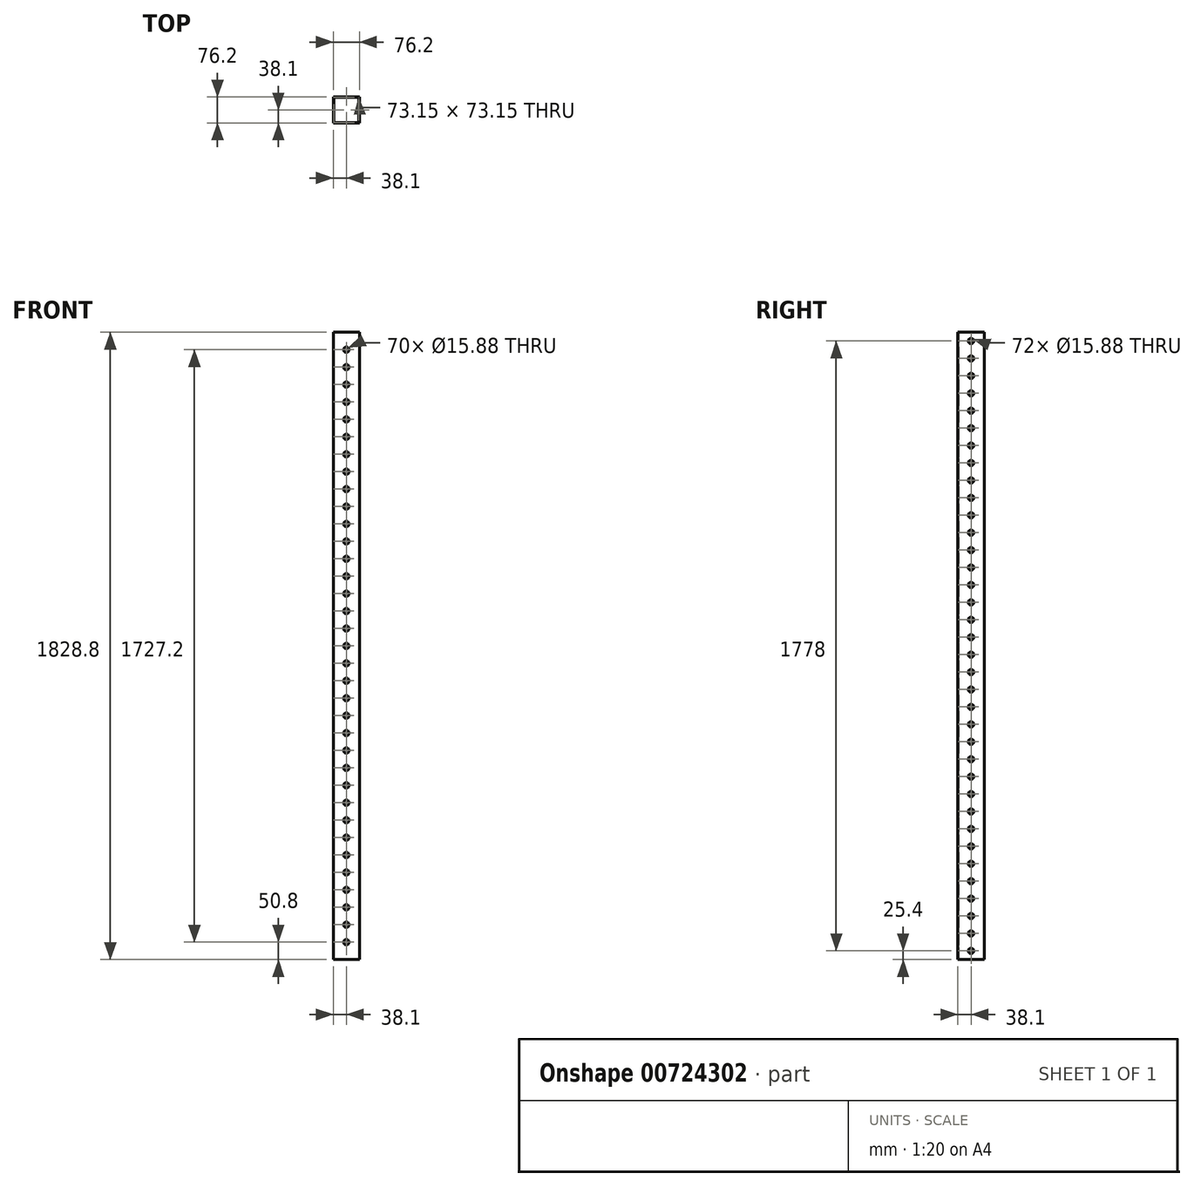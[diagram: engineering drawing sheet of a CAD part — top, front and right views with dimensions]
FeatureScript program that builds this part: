
annotation { "Feature Type Name" : "Feature", "Feature Type Description" : "" }
export const myFeature = defineFeature(function(context is Context, id is Id, definition is map)
    precondition{}
    {
        {
            var Q0;
            Q0=qCreatedBy(makeId("Top.planeOp"),FACE);
            var sketch = newSketch(context, id + "F0", { "sketchPlane" : qUnion([Q0])});
            skLineSegment(sketch, "E0.bottom", {"start": v(-38.1, -38.1) * mm, "end": v(38.1, -38.1) * mm});
            skLineSegment(sketch, "E0.top", {"start": v(-38.1, 38.1) * mm, "end": v(38.1, 38.1) * mm});
            skLineSegment(sketch, "E0.left", {"start": v(-38.1, -38.1) * mm, "end": v(-38.1, 38.1) * mm});
            skLineSegment(sketch, "E0.right", {"start": v(38.1, -38.1) * mm, "end": v(38.1, 38.1) * mm});
            skPoint(sketch, "E0.middle", {"position": v(0, 0) * mm});
            skLineSegment(sketch, "E1.bottom", {"start": v(-36.58, -36.58) * mm, "end": v(36.58, -36.58) * mm});
            skLineSegment(sketch, "E1.top", {"start": v(-36.58, 36.58) * mm, "end": v(36.58, 36.58) * mm});
            skLineSegment(sketch, "E1.left", {"start": v(-36.58, -36.58) * mm, "end": v(-36.58, 36.58) * mm});
            skLineSegment(sketch, "E1.right", {"start": v(36.58, -36.58) * mm, "end": v(36.58, 36.58) * mm});
            skSolve(sketch);
        }
        {
            var Q0;
            Q0=makeQuery(id+"F0.imprint","IMPRINT",FACE,{"disambiguationData":[TD([[makeQuery(id+"F0.imprint","IMPRINT",EDGE,{"derivedFrom":sQuery(id+"F0.wireOp",EDGE,"E0.bottom")}),1.0]])]});
            extrude(context, id + "F1", {"entities" : qUnion([Q0]), "depth" : 1828.8 * mm, "offsetDistance" : 25.4 * mm});
        }
        {
            var Q0;
            Q0=qCreatedBy(makeId("Front.planeOp"),FACE);
            cPlane(context, id + "F2", {"entities" : qUnion([Q0]), "cplaneType" : CPlaneType.OFFSET, "offset" : 76.2 * mm, "width" : 152.4 * mm, "height" : 152.4 * mm});
        }
        {
            var Q0;
            Q0=qCreatedBy(id+"F2.planeOp",FACE);
            var sketch = newSketch(context, id + "F3", { "sketchPlane" : qUnion([Q0])});
            skPoint(sketch, "E2", {"position": v(0, 50.8) * mm});
            skPoint(sketch, "E3.1.0.0", {"position": v(0, 101.6) * mm});
            skPoint(sketch, "E3.2.0.0", {"position": v(0, 152.4) * mm});
            skPoint(sketch, "E3.3.0.0", {"position": v(0, 203.2) * mm});
            skPoint(sketch, "E3.4.0.0", {"position": v(0, 254) * mm});
            skPoint(sketch, "E3.5.0.0", {"position": v(0, 304.8) * mm});
            skPoint(sketch, "E3.6.0.0", {"position": v(0, 355.6) * mm});
            skPoint(sketch, "E3.7.0.0", {"position": v(0, 406.4) * mm});
            skPoint(sketch, "E3.8.0.0", {"position": v(0, 457.2) * mm});
            skPoint(sketch, "E3.9.0.0", {"position": v(0, 508) * mm});
            skPoint(sketch, "E3.10.0.0", {"position": v(0, 558.8) * mm});
            skPoint(sketch, "E3.11.0.0", {"position": v(0, 609.6) * mm});
            skPoint(sketch, "E3.12.0.0", {"position": v(0, 660.4) * mm});
            skPoint(sketch, "E3.13.0.0", {"position": v(0, 711.2) * mm});
            skPoint(sketch, "E3.14.0.0", {"position": v(0, 762) * mm});
            skPoint(sketch, "E3.15.0.0", {"position": v(0, 812.8) * mm});
            skPoint(sketch, "E3.16.0.0", {"position": v(0, 863.6) * mm});
            skLineSegment(sketch, "E3.direction1", {"start": v(0, 50.8) * mm, "end": v(0, 101.6) * mm, "construction": true});
            skPoint(sketch, "E4.0.17.0", {"position": v(0, 914.4) * mm});
            skPoint(sketch, "E4.0.18.0", {"position": v(0, 965.2) * mm});
            skPoint(sketch, "E4.0.19.0", {"position": v(0, 1016) * mm});
            skPoint(sketch, "E4.0.20.0", {"position": v(0, 1066.8) * mm});
            skPoint(sketch, "E4.0.21.0", {"position": v(0, 1117.6) * mm});
            skPoint(sketch, "E4.0.22.0", {"position": v(0, 1168.4) * mm});
            skPoint(sketch, "E4.0.23.0", {"position": v(0, 1219.2) * mm});
            skPoint(sketch, "E4.0.24.0", {"position": v(0, 1270) * mm});
            skPoint(sketch, "E4.0.25.0", {"position": v(0, 1320.8) * mm});
            skPoint(sketch, "E4.0.26.0", {"position": v(0, 1371.6) * mm});
            skPoint(sketch, "E4.0.27.0", {"position": v(0, 1422.4) * mm});
            skPoint(sketch, "E4.0.28.0", {"position": v(0, 1473.2) * mm});
            skPoint(sketch, "E4.0.29.0", {"position": v(0, 1524) * mm});
            skPoint(sketch, "E4.0.30.0", {"position": v(0, 1574.8) * mm});
            skPoint(sketch, "E4.0.31.0", {"position": v(0, 1625.6) * mm});
            skPoint(sketch, "E4.0.32.0", {"position": v(0, 1676.4) * mm});
            skPoint(sketch, "E4.0.33.0", {"position": v(0, 1727.2) * mm});
            skPoint(sketch, "E5.0.34.0", {"position": v(0, 1778) * mm});
            skSolve(sketch);
        }
        {
            var Q0;
            Q0=qCreatedBy(makeId("Right.planeOp"),FACE);
            cPlane(context, id + "F4", {"entities" : qUnion([Q0]), "cplaneType" : CPlaneType.OFFSET, "offset" : 76.2 * mm, "width" : 152.4 * mm, "height" : 152.4 * mm});
        }
        {
            var Q0;
            Q0=qCreatedBy(id+"F4.planeOp",FACE);
            var sketch = newSketch(context, id + "F5", { "sketchPlane" : qUnion([Q0])});
            skPoint(sketch, "E6", {"position": v(0, 25.4) * mm});
            skPoint(sketch, "E7.1.0.0", {"position": v(0, 76.2) * mm});
            skPoint(sketch, "E7.2.0.0", {"position": v(0, 127) * mm});
            skPoint(sketch, "E7.3.0.0", {"position": v(0, 177.8) * mm});
            skPoint(sketch, "E7.4.0.0", {"position": v(0, 228.6) * mm});
            skPoint(sketch, "E7.5.0.0", {"position": v(0, 279.4) * mm});
            skPoint(sketch, "E7.6.0.0", {"position": v(0, 330.2) * mm});
            skPoint(sketch, "E7.7.0.0", {"position": v(0, 381) * mm});
            skPoint(sketch, "E7.8.0.0", {"position": v(0, 431.8) * mm});
            skPoint(sketch, "E7.9.0.0", {"position": v(0, 482.6) * mm});
            skPoint(sketch, "E7.10.0.0", {"position": v(0, 533.4) * mm});
            skPoint(sketch, "E7.11.0.0", {"position": v(0, 584.2) * mm});
            skPoint(sketch, "E7.12.0.0", {"position": v(0, 635) * mm});
            skPoint(sketch, "E7.13.0.0", {"position": v(0, 685.8) * mm});
            skPoint(sketch, "E7.14.0.0", {"position": v(0, 736.6) * mm});
            skPoint(sketch, "E7.15.0.0", {"position": v(0, 787.4) * mm});
            skPoint(sketch, "E7.16.0.0", {"position": v(0, 838.2) * mm});
            skPoint(sketch, "E7.17.0.0", {"position": v(0, 889) * mm});
            skLineSegment(sketch, "E7.direction1", {"start": v(0, 25.4) * mm, "end": v(0, 76.2) * mm, "construction": true});
            skPoint(sketch, "E8.0.18.0", {"position": v(0, 939.8) * mm});
            skPoint(sketch, "E8.0.19.0", {"position": v(0, 990.6) * mm});
            skPoint(sketch, "E8.0.20.0", {"position": v(0, 1041.4) * mm});
            skPoint(sketch, "E8.0.21.0", {"position": v(0, 1092.2) * mm});
            skPoint(sketch, "E8.0.22.0", {"position": v(0, 1143) * mm});
            skPoint(sketch, "E8.0.23.0", {"position": v(0, 1193.8) * mm});
            skPoint(sketch, "E8.0.24.0", {"position": v(0, 1244.6) * mm});
            skPoint(sketch, "E8.0.25.0", {"position": v(0, 1295.4) * mm});
            skPoint(sketch, "E8.0.26.0", {"position": v(0, 1346.2) * mm});
            skPoint(sketch, "E8.0.27.0", {"position": v(0, 1397) * mm});
            skPoint(sketch, "E8.0.28.0", {"position": v(0, 1447.8) * mm});
            skPoint(sketch, "E8.0.29.0", {"position": v(0, 1498.6) * mm});
            skPoint(sketch, "E8.0.30.0", {"position": v(0, 1549.4) * mm});
            skPoint(sketch, "E8.0.31.0", {"position": v(0, 1600.2) * mm});
            skPoint(sketch, "E8.0.32.0", {"position": v(0, 1651) * mm});
            skPoint(sketch, "E8.0.33.0", {"position": v(0, 1701.8) * mm});
            skPoint(sketch, "E8.0.34.0", {"position": v(0, 1752.6) * mm});
            skPoint(sketch, "E8.0.35.0", {"position": v(0, 1803.4) * mm});
            skSolve(sketch);
        }
        {
            var Q0;
            Q0=sQuery(id+"F5.wireOp",VERTEX,"E6");
            var Q1;
            Q1=sQuery(id+"F5.wireOp",VERTEX,"E7.1.0.0");
            var Q2;
            Q2=sQuery(id+"F5.wireOp",VERTEX,"E7.2.0.0");
            var Q3;
            Q3=sQuery(id+"F5.wireOp",VERTEX,"E7.3.0.0");
            var Q4;
            Q4=sQuery(id+"F5.wireOp",VERTEX,"E7.4.0.0");
            var Q5;
            Q5=sQuery(id+"F5.wireOp",VERTEX,"E7.5.0.0");
            var Q6;
            Q6=sQuery(id+"F5.wireOp",VERTEX,"E7.6.0.0");
            var Q7;
            Q7=sQuery(id+"F5.wireOp",VERTEX,"E7.7.0.0");
            var Q8;
            Q8=sQuery(id+"F5.wireOp",VERTEX,"E7.8.0.0");
            var Q9;
            Q9=sQuery(id+"F5.wireOp",VERTEX,"E7.9.0.0");
            var Q10;
            Q10=sQuery(id+"F5.wireOp",VERTEX,"E7.10.0.0");
            var Q11;
            Q11=sQuery(id+"F5.wireOp",VERTEX,"E7.11.0.0");
            var Q12;
            Q12=sQuery(id+"F5.wireOp",VERTEX,"E7.12.0.0");
            var Q13;
            Q13=sQuery(id+"F5.wireOp",VERTEX,"E7.13.0.0");
            var Q14;
            Q14=sQuery(id+"F5.wireOp",VERTEX,"E7.14.0.0");
            var Q15;
            Q15=sQuery(id+"F5.wireOp",VERTEX,"E7.15.0.0");
            var Q16;
            Q16=sQuery(id+"F5.wireOp",VERTEX,"E7.16.0.0");
            var Q17;
            Q17=sQuery(id+"F5.wireOp",VERTEX,"E7.17.0.0");
            var Q18;
            Q18=sQuery(id+"F3.wireOp",VERTEX,"E3.16.0.0");
            var Q19;
            Q19=sQuery(id+"F3.wireOp",VERTEX,"E3.15.0.0");
            var Q20;
            Q20=sQuery(id+"F3.wireOp",VERTEX,"E3.14.0.0");
            var Q21;
            Q21=sQuery(id+"F3.wireOp",VERTEX,"E3.13.0.0");
            var Q22;
            Q22=sQuery(id+"F3.wireOp",VERTEX,"E3.12.0.0");
            var Q23;
            Q23=sQuery(id+"F3.wireOp",VERTEX,"E3.11.0.0");
            var Q24;
            Q24=sQuery(id+"F3.wireOp",VERTEX,"E3.10.0.0");
            var Q25;
            Q25=sQuery(id+"F3.wireOp",VERTEX,"E3.9.0.0");
            var Q26;
            Q26=sQuery(id+"F3.wireOp",VERTEX,"E3.8.0.0");
            var Q27;
            Q27=sQuery(id+"F3.wireOp",VERTEX,"E3.7.0.0");
            var Q28;
            Q28=sQuery(id+"F3.wireOp",VERTEX,"E3.6.0.0");
            var Q29;
            Q29=sQuery(id+"F3.wireOp",VERTEX,"E3.5.0.0");
            var Q30;
            Q30=sQuery(id+"F3.wireOp",VERTEX,"E3.4.0.0");
            var Q31;
            Q31=sQuery(id+"F3.wireOp",VERTEX,"E3.3.0.0");
            var Q32;
            Q32=sQuery(id+"F3.wireOp",VERTEX,"E3.2.0.0");
            var Q33;
            Q33=sQuery(id+"F3.wireOp",VERTEX,"E3.1.0.0");
            var Q34;
            Q34=sQuery(id+"F3.wireOp",VERTEX,"E2");
            var Q35;
            Q35=sQuery(id+"F3.wireOp",VERTEX,"E4.0.17.0");
            var Q36;
            Q36=sQuery(id+"F5.wireOp",VERTEX,"E8.0.18.0");
            var Q37;
            Q37=sQuery(id+"F3.wireOp",VERTEX,"E4.0.18.0");
            var Q38;
            Q38=sQuery(id+"F5.wireOp",VERTEX,"E8.0.19.0");
            var Q39;
            Q39=sQuery(id+"F5.wireOp",VERTEX,"E8.0.20.0");
            var Q40;
            Q40=sQuery(id+"F5.wireOp",VERTEX,"E8.0.21.0");
            var Q41;
            Q41=sQuery(id+"F5.wireOp",VERTEX,"E8.0.22.0");
            var Q42;
            Q42=sQuery(id+"F5.wireOp",VERTEX,"E8.0.23.0");
            var Q43;
            Q43=sQuery(id+"F5.wireOp",VERTEX,"E8.0.24.0");
            var Q44;
            Q44=sQuery(id+"F5.wireOp",VERTEX,"E8.0.25.0");
            var Q45;
            Q45=sQuery(id+"F5.wireOp",VERTEX,"E8.0.26.0");
            var Q46;
            Q46=sQuery(id+"F5.wireOp",VERTEX,"E8.0.27.0");
            var Q47;
            Q47=sQuery(id+"F5.wireOp",VERTEX,"E8.0.28.0");
            var Q48;
            Q48=sQuery(id+"F5.wireOp",VERTEX,"E8.0.29.0");
            var Q49;
            Q49=sQuery(id+"F5.wireOp",VERTEX,"E8.0.30.0");
            var Q50;
            Q50=sQuery(id+"F5.wireOp",VERTEX,"E8.0.31.0");
            var Q51;
            Q51=sQuery(id+"F5.wireOp",VERTEX,"E8.0.32.0");
            var Q52;
            Q52=sQuery(id+"F5.wireOp",VERTEX,"E8.0.33.0");
            var Q53;
            Q53=sQuery(id+"F5.wireOp",VERTEX,"E8.0.34.0");
            var Q54;
            Q54=sQuery(id+"F5.wireOp",VERTEX,"E8.0.35.0");
            var Q55;
            Q55=sQuery(id+"F3.wireOp",VERTEX,"E5.0.34.0");
            var Q56;
            Q56=sQuery(id+"F3.wireOp",VERTEX,"E4.0.33.0");
            var Q57;
            Q57=sQuery(id+"F3.wireOp",VERTEX,"E4.0.32.0");
            var Q58;
            Q58=sQuery(id+"F3.wireOp",VERTEX,"E4.0.31.0");
            var Q59;
            Q59=sQuery(id+"F3.wireOp",VERTEX,"E4.0.30.0");
            var Q60;
            Q60=sQuery(id+"F3.wireOp",VERTEX,"E4.0.29.0");
            var Q61;
            Q61=sQuery(id+"F3.wireOp",VERTEX,"E4.0.28.0");
            var Q62;
            Q62=sQuery(id+"F3.wireOp",VERTEX,"E4.0.27.0");
            var Q63;
            Q63=sQuery(id+"F3.wireOp",VERTEX,"E4.0.26.0");
            var Q64;
            Q64=sQuery(id+"F3.wireOp",VERTEX,"E4.0.25.0");
            var Q65;
            Q65=sQuery(id+"F3.wireOp",VERTEX,"E4.0.24.0");
            var Q66;
            Q66=sQuery(id+"F3.wireOp",VERTEX,"E4.0.23.0");
            var Q67;
            Q67=sQuery(id+"F3.wireOp",VERTEX,"E4.0.22.0");
            var Q68;
            Q68=sQuery(id+"F3.wireOp",VERTEX,"E4.0.21.0");
            var Q69;
            Q69=sQuery(id+"F3.wireOp",VERTEX,"E4.0.20.0");
            var Q70;
            Q70=sQuery(id+"F3.wireOp",VERTEX,"E4.0.19.0");
            var Q71;
            Q71=makeQuery(id+"F1.opExtrude","SWEPT_BODY",BODY,{"disambiguationData":[OSD([sQuery(id+"F0.wireOp",EDGE,"E0.bottom"),sQuery(id+"F0.wireOp",EDGE,"E0.top"),sQuery(id+"F0.wireOp",EDGE,"E0.left"),sQuery(id+"F0.wireOp",EDGE,"E0.right"),sQuery(id+"F0.wireOp",EDGE,"E1.bottom"),sQuery(id+"F0.wireOp",EDGE,"E1.top"),sQuery(id+"F0.wireOp",EDGE,"E1.left"),sQuery(id+"F0.wireOp",EDGE,"E1.right")])]});
            hole(context, id + "F6", {"style" : HoleStyle.SIMPLE, "endStyle" : HoleEndStyle.THROUGH, "holeDiameter" : 15.88 * mm, "majorDiameter" : 6.35 * mm, "isTappedThrough" : true, "tappedDepth" : 12.7 * mm, "tapClearance" : 3, "locations" : qUnion([Q0, Q1, Q2, Q3, Q4, Q5, Q6, Q7, Q8, Q9, Q10, Q11, Q12, Q13, Q14, Q15, Q16, Q17, Q18, Q19, Q20, Q21, Q22, Q23, Q24, Q25, Q26, Q27, Q28, Q29, Q30, Q31, Q32, Q33, Q34, Q35, Q36, Q37, Q38, Q39, Q40, Q41, Q42, Q43, Q44, Q45, Q46, Q47, Q48, Q49, Q50, Q51, Q52, Q53, Q54, Q55, Q56, Q57, Q58, Q59, Q60, Q61, Q62, Q63, Q64, Q65, Q66, Q67, Q68, Q69, Q70]), "scope" : qUnion([Q71])});
        }
    });
